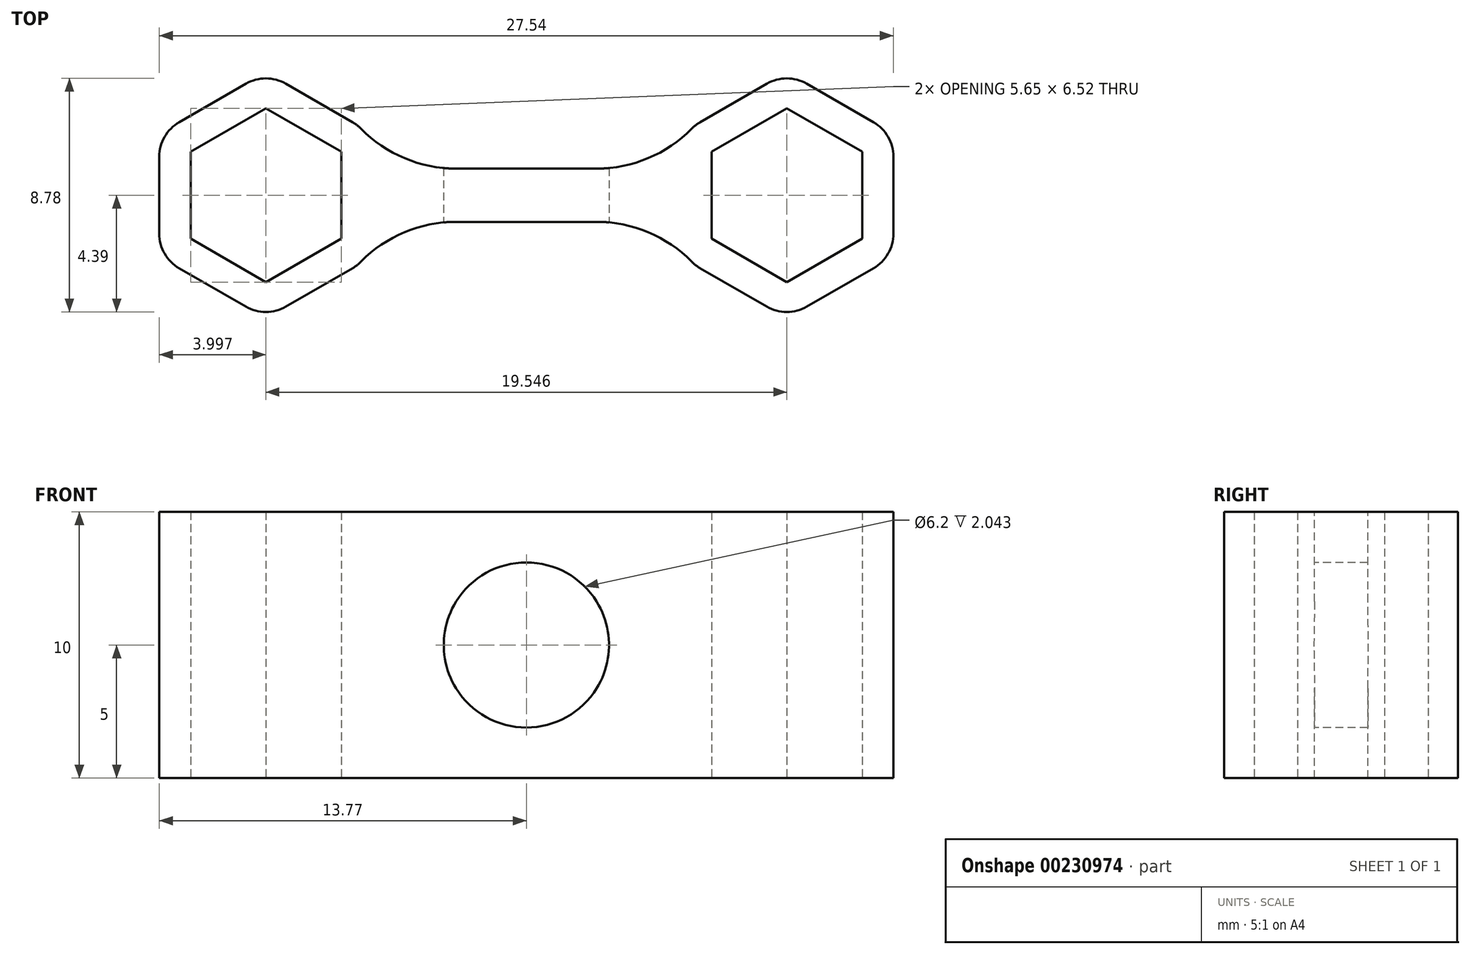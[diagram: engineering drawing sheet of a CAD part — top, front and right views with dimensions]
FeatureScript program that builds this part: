
annotation { "Feature Type Name" : "Feature", "Feature Type Description" : "" }
export const myFeature = defineFeature(function(context is Context, id is Id, definition is map)
    precondition{}
    {
        {
            var Q0;
            Q0=qCreatedBy(makeId("Top.planeOp"),FACE);
            var sketch = newSketch(context, id + "F0", { "sketchPlane" : qUnion([Q0])});
            skPoint(sketch, "E0.middle", {"position": v(0, 0) * mm});
            skCircle(sketch, "E1.cCircle", {"center": v(-9.77, 0) * mm, "radius": 2.83 * mm, "construction": true});
            skLineSegment(sketch, "E1.0", {"start": v(-6.95, 1.63) * mm, "end": v(-6.95, -1.63) * mm});
            skLineSegment(sketch, "E1.1", {"start": v(-6.95, -1.63) * mm, "end": v(-9.77, -3.26) * mm});
            skLineSegment(sketch, "E1.2", {"start": v(-9.77, -3.26) * mm, "end": v(-12.6, -1.63) * mm});
            skLineSegment(sketch, "E1.3", {"start": v(-12.6, -1.63) * mm, "end": v(-12.6, 1.63) * mm});
            skLineSegment(sketch, "E1.4", {"start": v(-12.6, 1.63) * mm, "end": v(-9.77, 3.26) * mm});
            skLineSegment(sketch, "E1.5", {"start": v(-9.77, 3.26) * mm, "end": v(-6.95, 1.63) * mm});
            skPoint(sketch, "E1.0.midPoint", {"position": v(-6.95, 0) * mm});
            skCircle(sketch, "E2.cCircle", {"center": v(-9.77, 0) * mm, "radius": 4 * mm, "construction": true});
            skLineSegment(sketch, "E2.0", {"start": v(-5.77, 2.3) * mm, "end": v(-5.77, -2.3) * mm});
            skLineSegment(sketch, "E2.1", {"start": v(-5.77, -2.3) * mm, "end": v(-9.77, -4.62) * mm});
            skLineSegment(sketch, "E2.2", {"start": v(-9.77, -4.62) * mm, "end": v(-13.77, -2.3) * mm});
            skLineSegment(sketch, "E2.3", {"start": v(-13.77, -2.3) * mm, "end": v(-13.77, 2.3) * mm});
            skLineSegment(sketch, "E2.4", {"start": v(-13.77, 2.3) * mm, "end": v(-9.77, 4.62) * mm});
            skLineSegment(sketch, "E2.5", {"start": v(-9.77, 4.62) * mm, "end": v(-5.77, 2.3) * mm});
            skPoint(sketch, "E2.0.midPoint", {"position": v(-5.77, 0) * mm});
            skPoint(sketch, "E3.MirrorP", {"position": v(5.77, 0) * mm});
            skCircle(sketch, "E4.MirrorC", {"center": v(9.77, 0) * mm, "radius": 4 * mm, "construction": true});
            skLineSegment(sketch, "E5.MirrorCS", {"start": v(13.77, 2.3) * mm, "end": v(9.77, 4.62) * mm});
            skLineSegment(sketch, "E6.MirrorCS", {"start": v(13.77, -2.3) * mm, "end": v(13.77, 2.3) * mm});
            skLineSegment(sketch, "E7.MirrorCS", {"start": v(9.77, 3.26) * mm, "end": v(6.95, 1.63) * mm});
            skLineSegment(sketch, "E8.MirrorCS", {"start": v(5.77, 2.3) * mm, "end": v(5.77, -2.3) * mm});
            skLineSegment(sketch, "E9.MirrorCS", {"start": v(12.6, 1.63) * mm, "end": v(9.77, 3.26) * mm});
            skLineSegment(sketch, "E10.MirrorCS", {"start": v(6.95, 1.63) * mm, "end": v(6.95, -1.63) * mm});
            skLineSegment(sketch, "E11.MirrorCS", {"start": v(12.6, -1.63) * mm, "end": v(12.6, 1.63) * mm});
            skLineSegment(sketch, "E12.MirrorCS", {"start": v(6.95, -1.63) * mm, "end": v(9.77, -3.26) * mm});
            skLineSegment(sketch, "E13.MirrorCS", {"start": v(9.77, 4.62) * mm, "end": v(5.77, 2.3) * mm});
            skPoint(sketch, "E14.MirrorP", {"position": v(6.95, 0) * mm});
            skLineSegment(sketch, "E15.MirrorCS", {"start": v(9.77, -3.26) * mm, "end": v(12.6, -1.63) * mm});
            skCircle(sketch, "E16.MirrorC", {"center": v(9.77, 0) * mm, "radius": 2.83 * mm, "construction": true});
            skLineSegment(sketch, "E17.MirrorCS", {"start": v(9.77, -4.62) * mm, "end": v(13.77, -2.3) * mm});
            skLineSegment(sketch, "E18.MirrorCS", {"start": v(5.77, -2.3) * mm, "end": v(9.77, -4.62) * mm});
            skLineSegment(sketch, "E19", {"start": v(0, 1) * mm, "end": v(-5.77, 1) * mm});
            skLineSegment(sketch, "E20", {"start": v(0, -1) * mm, "end": v(-5.77, -1) * mm});
            skLineSegment(sketch, "E21.MirrorCS", {"start": v(0, 1) * mm, "end": v(5.77, 1) * mm});
            skLineSegment(sketch, "E22.MirrorCS", {"start": v(0, -1) * mm, "end": v(5.77, -1) * mm});
            skSolve(sketch);
        }
        {
            var Q0;
            Q0=makeQuery(id+"F0.imprint","IMPRINT",FACE,{"disambiguationData":[TD([[makeQuery(id+"F0.imprint","IMPRINT",EDGE,{"derivedFrom":sQuery(id+"F0.wireOp",EDGE,"E2.0")}),1.0]])]});
            var Q1;
            Q1=makeQuery(id+"F0.imprint","IMPRINT",FACE,{"disambiguationData":[TD([[makeQuery(id+"F0.imprint","IMPRINT",EDGE,{"derivedFrom":sQuery(id+"F0.wireOp",EDGE,"E1.0")}),1.0]])]});
            var Q2;
            Q2=makeQuery(id+"F0.imprint","IMPRINT",FACE,{"disambiguationData":[TD([[makeQuery(id+"F0.imprint","IMPRINT",EDGE,{"derivedFrom":sQuery(id+"F0.wireOp",EDGE,"E5.MirrorCS")}),1.0]])]});
            extrude(context, id + "F1", {"entities" : qUnion([Q0, Q1, Q2]), "depth" : 10 * mm, "offsetDistance" : 25 * mm});
        }
        {
            var Q0;
            Q0=makeQuery(id+"F1.opExtrude","SWEPT_EDGE",EDGE,{"disambiguationData":[OSD([sQuery(id+"F0.wireOp",EDGE,"E2.1"),sQuery(id+"F0.wireOp",EDGE,"E2.2")])]});
            var Q1;
            Q1=makeQuery(id+"F1.opExtrude","SWEPT_EDGE",EDGE,{"disambiguationData":[OSD([sQuery(id+"F0.wireOp",EDGE,"E2.2"),sQuery(id+"F0.wireOp",EDGE,"E2.3")])]});
            var Q2;
            Q2=makeQuery(id+"F1.opExtrude","SWEPT_EDGE",EDGE,{"disambiguationData":[OSD([sQuery(id+"F0.wireOp",EDGE,"E2.3"),sQuery(id+"F0.wireOp",EDGE,"E2.4")])]});
            var Q3;
            Q3=makeQuery(id+"F1.opExtrude","SWEPT_EDGE",EDGE,{"disambiguationData":[OSD([sQuery(id+"F0.wireOp",EDGE,"E2.4"),sQuery(id+"F0.wireOp",EDGE,"E2.5")])]});
            var Q4;
            Q4=makeQuery(id+"F1.opExtrude","SWEPT_EDGE",EDGE,{"disambiguationData":[OSD([sQuery(id+"F0.wireOp",EDGE,"E2.0"),sQuery(id+"F0.wireOp",EDGE,"E2.5"),sQuery(id+"F0.wireOp",EDGE,"i2exbP7Y-8fLs-IeNX-XnE8-nkZZ6vlEEHiD")])]});
            var Q5;
            Q5=makeQuery(id+"F1.opExtrude","SWEPT_EDGE",EDGE,{"disambiguationData":[OSD([sQuery(id+"F0.wireOp",EDGE,"E2.0"),sQuery(id+"F0.wireOp",EDGE,"E2.1"),sQuery(id+"F0.wireOp",EDGE,"WyHdD91X-kX72-26RG-egUu-OfX4yfC9RdaF")])]});
            var Q6;
            Q6=makeQuery(id+"F1.opExtrude","SWEPT_EDGE",EDGE,{"disambiguationData":[OSD([sQuery(id+"F0.wireOp",EDGE,"E8.MirrorCS"),sQuery(id+"F0.wireOp",EDGE,"E13.MirrorCS"),sQuery(id+"F0.wireOp",EDGE,"ff27c6cb-e7f7-46ed-81e3-513e21cccfa90.MirrorCS")])]});
            var Q7;
            Q7=makeQuery(id+"F1.opExtrude","SWEPT_EDGE",EDGE,{"disambiguationData":[OSD([sQuery(id+"F0.wireOp",EDGE,"E5.MirrorCS"),sQuery(id+"F0.wireOp",EDGE,"E13.MirrorCS")])]});
            var Q8;
            Q8=makeQuery(id+"F1.opExtrude","SWEPT_EDGE",EDGE,{"disambiguationData":[OSD([sQuery(id+"F0.wireOp",EDGE,"E5.MirrorCS"),sQuery(id+"F0.wireOp",EDGE,"E6.MirrorCS")])]});
            var Q9;
            Q9=makeQuery(id+"F1.opExtrude","SWEPT_EDGE",EDGE,{"disambiguationData":[OSD([sQuery(id+"F0.wireOp",EDGE,"E6.MirrorCS"),sQuery(id+"F0.wireOp",EDGE,"E17.MirrorCS")])]});
            var Q10;
            Q10=makeQuery(id+"F1.opExtrude","SWEPT_EDGE",EDGE,{"disambiguationData":[OSD([sQuery(id+"F0.wireOp",EDGE,"E17.MirrorCS"),sQuery(id+"F0.wireOp",EDGE,"E18.MirrorCS")])]});
            var Q11;
            Q11=makeQuery(id+"F1.opExtrude","SWEPT_EDGE",EDGE,{"disambiguationData":[OSD([sQuery(id+"F0.wireOp",EDGE,"E8.MirrorCS"),sQuery(id+"F0.wireOp",EDGE,"E18.MirrorCS"),sQuery(id+"F0.wireOp",EDGE,"12a32369-1642-42fb-84ed-d682b6364e350.MirrorCS")])]});
            fillet(context, id + "F2", {"entities" : qUnion([Q0, Q1, Q2, Q3, Q4, Q5, Q6, Q7, Q8, Q9, Q10, Q11]), "radius" : 1.5 * mm, "tangentPropagation" : true, "allowEdgeOverflow" : false});
        }
        {
            var Q0;
            Q0=makeQuery(id+"F1.opExtrude","SWEPT_FACE",FACE,{"disambiguationData":[OSD([sQuery(id+"F0.wireOp",EDGE,"E20"),sQuery(id+"F0.wireOp",EDGE,"E22.MirrorCS")])]});
            var sketch = newSketch(context, id + "F3", { "sketchPlane" : qUnion([Q0])});
            skCircle(sketch, "E23", {"center": v(0, 5) * mm, "radius": 3.1 * mm});
            skSolve(sketch);
        }
        {
            var Q0;
            Q0=makeQuery(id+"F1.opExtrude","SWEPT_EDGE",EDGE,{"disambiguationData":[OSD([sQuery(id+"F0.wireOp",EDGE,"E2.0"),sQuery(id+"F0.wireOp",EDGE,"E20")])]});
            var Q1;
            Q1=makeQuery(id+"F1.opExtrude","SWEPT_EDGE",EDGE,{"disambiguationData":[OSD([sQuery(id+"F0.wireOp",EDGE,"E2.0"),sQuery(id+"F0.wireOp",EDGE,"E19")])]});
            var Q2;
            Q2=makeQuery(id+"F1.opExtrude","SWEPT_EDGE",EDGE,{"disambiguationData":[OSD([sQuery(id+"F0.wireOp",EDGE,"E8.MirrorCS"),sQuery(id+"F0.wireOp",EDGE,"E21.MirrorCS")])]});
            var Q3;
            Q3=makeQuery(id+"F1.opExtrude","SWEPT_EDGE",EDGE,{"disambiguationData":[OSD([sQuery(id+"F0.wireOp",EDGE,"E8.MirrorCS"),sQuery(id+"F0.wireOp",EDGE,"E22.MirrorCS")])]});
            fillet(context, id + "F4", {"entities" : qUnion([Q0, Q1, Q2, Q3]), "radius" : 5 * mm, "tangentPropagation" : true, "allowEdgeOverflow" : false});
        }
        {
            var Q0;
            Q0=makeQuery(id+"F3.imprint","IMPRINT",FACE,{"disambiguationData":[TD([[makeQuery(id+"F3.imprint","IMPRINT",EDGE,{"derivedFrom":sQuery(id+"F3.wireOp",EDGE,"E23")}),1.0]])]});
            extrude(context, id + "F5", {"entities" : qUnion([Q0]), "operationType" : NewBodyOperationType.REMOVE, "oppositeDirection" : true, "depth" : 5 * mm, "offsetDistance" : 25 * mm, "symmetric" : true});
        }
    });
